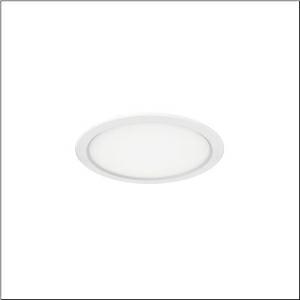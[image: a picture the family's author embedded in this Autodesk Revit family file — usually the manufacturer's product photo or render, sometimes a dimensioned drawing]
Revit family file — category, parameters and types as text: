
# Revit family: lunis_41_eco_51ds107f44b
name_source: partatom
category: Lighting Fixtures
units: mm (PartAtom-declared; Revit-internal decimal feet)

## family parameters
Cut with Voids When Loaded = No
Host = Face
Light Source = No
Part Type = Normal
Room Calculation Point = No
Round Connector Dimension = Use Diameter
Shared = No

## types (1)
- Lunis 41 Eco (1 x LED, 2300 lm, 17.5 W, 4000K)
    Apparent Load = 18 VA
    CIE Flux Codes = 47 80 97 100 100
    Color Rendering = 80
    Color Temperature = 4000K
    Default Elevation = 1800 mm
    Description = Lunis 41,  Eco, downlight, light emission: direct distribution, LED rated luminous flux: 2.300lm, light colour: 840, mains connection: 230V, AC, 50/60Hz, housing, round, of aluminium, coated, traffic white (RAL 9016), diameter: 216mm, recess depth: 58mm, protection rating (complete): IP20, protection rating (on room side): IP40, insulation class (complete): insulation class II (safety insulation), certification: CE, permissible ambient temperature for indoor applications: -20..+40°C, packaging unit: 1 piece
    Height = 0 mm  [stored 0 ft]
    Lamp = 1 x LED
    Lamp Light Flux = 2300 lm
    Lamp Power = 17.5 W
    Lamp count = 1
    Length = 216 mm
    Luminous efficacy = 131 lm/W
    Manufacturer = Siteco
    ModVariant = No
    Model = 51DS107F44B
    Mounting Place = Ceiling
    Mounting Type = Recessed
    Number of Poles = 1
    OnlyDefault = Yes
    Power Factor = 1
    Product Name = Lunis 41 Eco
    Product group = downlight
    ProductGroupID = 400
    Protection Class = Protection class II
    Protection Degree = IP 20
    RLX_Detail_Level = 1
    RLX_Emergency_Light_Flux = 0 lm
    RLX_Emergency_Type = 0
    RLX_Emergency_Type_DB = No
    RlxData = <blob elided: 10233 chars, md5=11b950a8>
    Socket = socket
    Standby Power = 0 W
    System Light Flux = 2300 lm
    System Power = 18 W
    Type Comments = Product without accessories
    Type Image = l_1345914.jpg
    URL = http://relux.com
    VarID = ---
    Voltage = 0 V
    Weight = 0.00 kg
    Width = 0 mm  [stored 0 ft]

note: [stored X ft] marks values corroborated as IEEE doubles in the binary element streams (Revit-internal decimal feet)

## geometry (parser evidence)
native form markers: Sweep x9
no freeform markers — native parametric forms only
